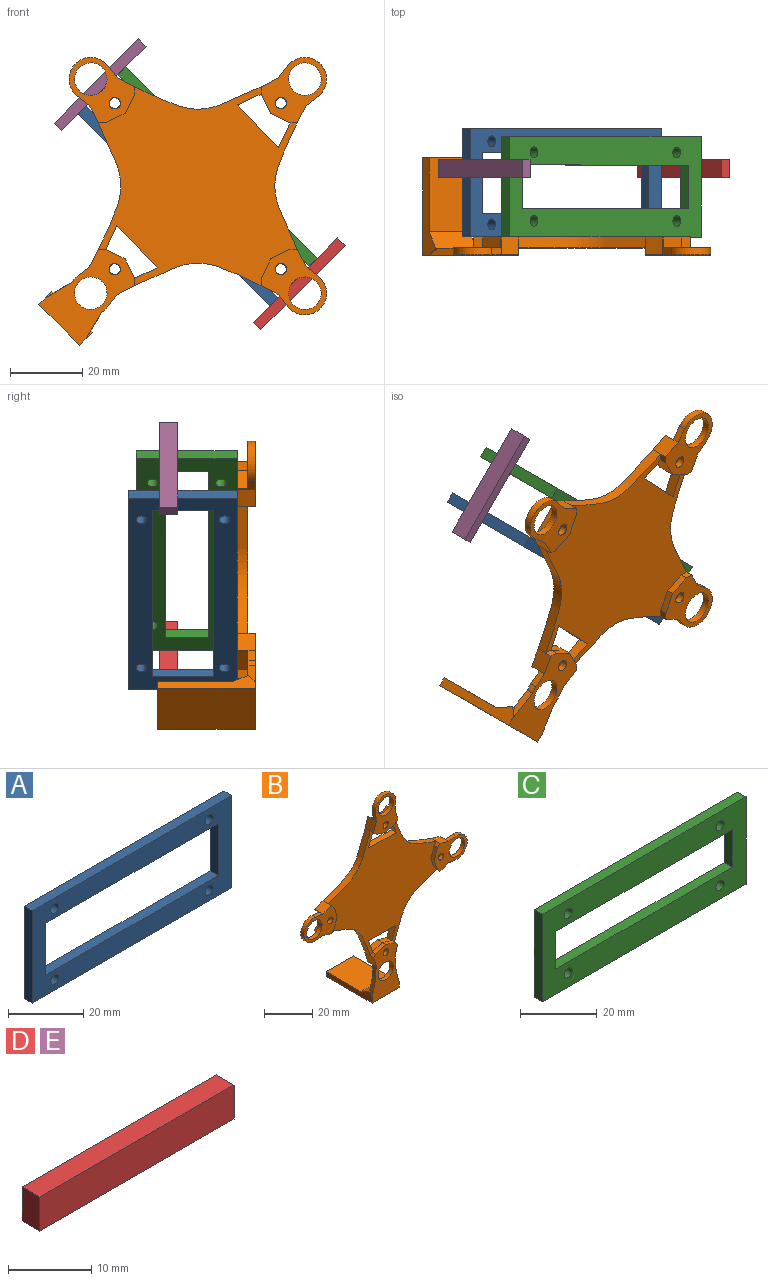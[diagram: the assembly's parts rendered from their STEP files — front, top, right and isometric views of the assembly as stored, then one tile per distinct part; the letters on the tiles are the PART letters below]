
ASSEMBLY  parts=5 mates=4
PART A: 14 faces, bbox 75x3x30 mm
  f0: plane 65x3mm, normal (0,0,-1), area 195mm2, adj f1,f11,f12,f13
  f1: plane 16.92x3mm, normal (-1,0,0), area 50.7mm2, adj f0,f2,f12,f13
  f2: plane 65x3mm, normal (0,0,1), area 195mm2, adj f1,f11,f12,f13
  f3: plane 30x3mm, normal (1,0,0), area 90mm2, adj f4,f10,f12,f13
  f4: plane 75x3mm, normal (0,0,1), area 225mm2, adj f3,f5,f12,f13
  f5: plane 30x3mm, normal (-1,0,0), area 90mm2, adj f4,f10,f12,f13
  f6: cylinder r=1.5mm len=3mm, axis (0,1,0), area 28.3mm2, adj f12,f13
  f7: cylinder r=1.5mm len=3mm, axis (0,1,0), area 28.3mm2, adj f12,f13
  f8: cylinder r=1.5mm len=3mm, axis (0,1,0), area 28.3mm2, adj f12,f13
  f9: cylinder r=1.5mm len=3mm, axis (0,1,0), area 28.3mm2, adj f12,f13
  f10: plane 75x3mm, normal (0,0,-1), area 225mm2, adj f3,f5,f12,f13
  f11: plane 16.92x3mm, normal (1,0,0), area 50.7mm2, adj f0,f2,f12,f13
  f12: plane 75x30mm, normal (0,-1,0), area 1122.2mm2, adj f0,f1,f2,f3,f4,f5,f6,f7
  f13: plane 75x30mm, normal (0,1,0), area 1122.2mm2, adj f0,f1,f2,f3,f4,f5,f6,f7
PART B: 98 faces, bbox 95.8x27x102.2 mm
  f0: plane 14.7x13.89mm, normal (0,1,0), area 102.7mm2, adj f1,f2,f4,f24,f25,f26,f59,f60
  f1: plane 8.46x2.17mm, normal (0.97,0,0.25), area 14.7mm2, adj f0,f4,f68,f95,f97
  f2: plane 8.46x2.17mm, normal (-0.97,0,0.25), area 14.7mm2, adj f0,f60,f68,f96,f97
  f3: plane 20.47x16mm, normal (0,0,1), area 327.5mm2, adj f91,f92,f94,f97
  f4: cylinder r=6mm len=2.08mm, axis (0,1,0), area 4.2mm2, adj f0,f1,f61,f68
  f5: plane 3.18x3.18mm, normal (0,-1,0), area 0.8mm2, adj f43,f84
  f6: plane 3.18x3.18mm, normal (0,-1,0), area 0.8mm2, adj f45,f77
  f7: plane 63.64x63.64mm, normal (0,-1,0), area 2022.9mm2, adj f10,f16,f22,f28,f34,f35,f36,f37
  f8: plane 3.18x3.18mm, normal (0,-1,0), area 0.8mm2, adj f44,f65
  f9: plane 3.18x3.18mm, normal (0,-1,0), area 0.8mm2, adj f46,f53
  f10: extruded ~24.75x24.75mm, area 112.2mm2, adj f7,f11,f47,f48
  f11: plane 5.15x5mm, normal (0.96,0,0.3), area 26.9mm2, adj f10,f12,f48,f82,f83,f87
  f12: plane 3x1.94mm, normal (-0.64,0,0.77), area 7.6mm2, adj f11,f13,f48,f88
  f13: plane 7.07x3mm, normal (0,0,1), area 21.2mm2, adj f12,f14,f48,f88
  f14: plane 3x1.94mm, normal (0.64,0,0.77), area 7.6mm2, adj f13,f15,f48,f88
  f15: plane 5.15x5mm, normal (-0.96,0,0.3), area 26.9mm2, adj f14,f16,f48,f80,f81,f87
  f16: extruded ~24.75x24.75mm, area 112.2mm2, adj f7,f15,f17,f48
  f17: plane 5.15x5mm, normal (-0.3,0,0.96), area 26.9mm2, adj f16,f18,f48,f49,f54,f56
  f18: plane 3x1.94mm, normal (-0.77,0,-0.64), area 7.6mm2, adj f17,f19,f48,f57
  f19: plane 7.07x3mm, normal (-1,0,0), area 21.2mm2, adj f18,f20,f48,f57
  f20: plane 3x1.94mm, normal (-0.77,0,0.64), area 7.6mm2, adj f19,f21,f48,f57
  f21: plane 5.15x5mm, normal (-0.3,0,-0.96), area 26.9mm2, adj f20,f22,f48,f51,f52,f56
  f22: extruded ~24.75x24.75mm, area 112.2mm2, adj f7,f21,f23,f48
  f23: plane 5.15x5mm, normal (-0.96,0,-0.3), area 26.9mm2, adj f22,f24,f48,f59,f66,f68
  f24: plane 3x1.94mm, normal (0.64,0,-0.77), area 7.6mm2, adj f0,f23,f25,f48
  f25: plane 7.07x3mm, normal (0,0,-1), area 21.2mm2, adj f0,f24,f26,f48
  f26: plane 3x1.94mm, normal (-0.64,0,-0.77), area 7.6mm2, adj f0,f25,f27,f48
  f27: plane 5.15x5mm, normal (0.96,0,-0.3), area 26.9mm2, adj f26,f28,f48,f61,f62,f68
  f28: extruded ~24.75x24.75mm, area 112.2mm2, adj f7,f27,f29,f48
  f29: plane 5.15x5mm, normal (0.3,0,-0.96), area 26.9mm2, adj f28,f30,f48,f73,f74,f79
  f30: plane 3x1.94mm, normal (0.77,0,0.64), area 7.6mm2, adj f29,f31,f48,f69
  f31: plane 7.07x3mm, normal (1,0,0), area 21.2mm2, adj f30,f32,f48,f69
  f32: plane 3x1.94mm, normal (0.77,0,-0.64), area 7.6mm2, adj f31,f47,f48,f69
  f33: plane 5.66x3mm, normal (-0.3,0,0.95), area 17.8mm2, adj f34,f42,f48,f58
  f34: plane 6.88x3mm, normal (0.94,0,0.34), area 22mm2, adj f7,f33,f48,f90
  f35: plane 5.66x2mm, normal (0.95,0,-0.32), area 11.9mm2, adj f7,f36,f52,f56
  f36: plane 5.66x2mm, normal (0.95,0,0.32), area 11.9mm2, adj f7,f35,f54,f56
  f37: plane 6.73x3mm, normal (0.94,0,-0.34), area 21.5mm2, adj f7,f38,f48,f89
  f38: plane 5.66x5mm, normal (-0.32,0,-0.95), area 29.8mm2, adj f37,f39,f48,f81,f87
  f39: plane 5.66x5mm, normal (0.32,0,-0.95), area 29.8mm2, adj f38,f40,f48,f82,f87
  f40: plane 7.16x3mm, normal (-0.94,0,-0.34), area 22.9mm2, adj f7,f39,f48,f89
  f41: plane 6.53x3mm, normal (-0.94,0,0.34), area 20.8mm2, adj f7,f42,f48,f90
  f42: plane 5.66x3mm, normal (0.3,0,0.95), area 17.8mm2, adj f33,f41,f48,f58
  f43: cylinder r=1.5mm len=3mm, axis (0,1,0), area 28.3mm2, adj f5,f48
  f44: cylinder r=1.5mm len=3mm, axis (0,1,0), area 28.3mm2, adj f8,f48
  f45: cylinder r=1.5mm len=3mm, axis (0,1,0), area 28.3mm2, adj f6,f48
  f46: cylinder r=1.5mm len=3mm, axis (0,1,0), area 28.3mm2, adj f9,f48
  f47: plane 5.15x5mm, normal (0.3,0,0.96), area 26.9mm2, adj f10,f32,f48,f70,f76,f79
  f48: plane 73.93x73.93mm, normal (0,1,0), area 2309.4mm2, adj f10,f11,f12,f13,f14,f15,f16,f17
  f49: plane 4.28x2mm, normal (0.11,0,0.99), area 8.6mm2, adj f17,f50,f56,f57
  f50: cylinder r=6mm len=12mm, axis (0,1,0), area 40.4mm2, adj f49,f51,f56,f57
  f51: plane 4.28x2mm, normal (0.11,0,-0.99), area 8.6mm2, adj f21,f50,f56,f57
  f52: plane 2x1.41mm, normal (0.71,0,-0.71), area 4mm2, adj f7,f21,f35,f56
  f53: cylinder r=1.59mm len=3.18mm, axis (0,1,0), area 20mm2, adj f9,f56
  f54: plane 2x1.41mm, normal (0.71,0,0.71), area 4mm2, adj f7,f17,f36,f56
  f55: cylinder r=4.5mm len=9mm, axis (0,1,0), area 56.5mm2, adj f56,f57
  f56: plane 19.42x14.14mm, normal (0,-1,0), area 135.4mm2, adj f17,f21,f35,f36,f49,f50,f51,f52
  f57: plane 12.57x12mm, normal (0,1,0), area 64.5mm2, adj f18,f19,f20,f49,f50,f51,f55
  f58: plane 11.31x1.91mm, normal (0,1,0), area 0.6mm2, adj f33,f42,f63,f64
  f59: plane 4.28x2mm, normal (-0.99,0,0.11), area 8.6mm2, adj f0,f23,f60,f68
  f60: cylinder r=6mm len=2.08mm, axis (0,1,0), area 4.2mm2, adj f0,f2,f59,f68
  f61: plane 4.28x2mm, normal (0.99,0,0.11), area 8.6mm2, adj f0,f4,f27,f68
  f62: plane 2x1.41mm, normal (0.71,0,0.71), area 4mm2, adj f7,f27,f63,f68
  f63: plane 5.66x2mm, normal (0.32,0,0.95), area 11.9mm2, adj f58,f62,f64,f68
  f64: plane 5.66x2mm, normal (-0.32,0,0.95), area 11.9mm2, adj f58,f63,f66,f68
  f65: cylinder r=1.59mm len=3.18mm, axis (0,1,0), area 20mm2, adj f8,f68
  f66: plane 2x1.41mm, normal (-0.71,0,0.71), area 4mm2, adj f7,f23,f64,f68
  f67: cylinder r=4.5mm len=9mm, axis (0,1,0), area 56.5mm2, adj f0,f68
  f68: plane 25.79x16mm, normal (0,-1,0), area 252.6mm2, adj f1,f2,f4,f23,f27,f59,f60,f61
  f69: plane 12.57x12mm, normal (0,1,0), area 64.5mm2, adj f30,f31,f32,f74,f75,f76,f78
  f70: plane 2x1.41mm, normal (-0.71,0,0.71), area 4mm2, adj f7,f47,f71,f79
  f71: plane 5.66x2mm, normal (-0.95,0,0.32), area 11.9mm2, adj f7,f70,f72,f79
  f72: plane 5.66x2mm, normal (-0.95,0,-0.32), area 11.9mm2, adj f7,f71,f73,f79
  f73: plane 2x1.41mm, normal (-0.71,0,-0.71), area 4mm2, adj f7,f29,f72,f79
  f74: plane 4.28x2mm, normal (-0.11,0,-0.99), area 8.6mm2, adj f29,f69,f75,f79
  f75: cylinder r=6mm len=12mm, axis (0,1,0), area 40.4mm2, adj f69,f74,f76,f79
  f76: plane 4.28x2mm, normal (-0.11,0,0.99), area 8.6mm2, adj f47,f69,f75,f79
  f77: cylinder r=1.59mm len=3.18mm, axis (0,1,0), area 20mm2, adj f6,f79
  f78: cylinder r=4.5mm len=9mm, axis (0,1,0), area 56.5mm2, adj f69,f79
  f79: plane 19.42x14.14mm, normal (0,-1,0), area 135.4mm2, adj f29,f47,f70,f71,f72,f73,f74,f75
  f80: plane 4.28x2mm, normal (-0.99,0,-0.11), area 8.6mm2, adj f15,f85,f87,f88
  f81: plane 2x1.41mm, normal (-0.71,0,-0.71), area 4mm2, adj f7,f15,f38,f87
  f82: plane 2x1.41mm, normal (0.71,0,-0.71), area 4mm2, adj f7,f11,f39,f87
  f83: plane 4.28x2mm, normal (0.99,0,-0.11), area 8.6mm2, adj f11,f85,f87,f88
  f84: cylinder r=1.59mm len=3.18mm, axis (0,1,0), area 20mm2, adj f5,f87
  f85: cylinder r=6mm len=12mm, axis (0,1,0), area 40.4mm2, adj f80,f83,f87,f88
  f86: cylinder r=4.5mm len=9mm, axis (0,1,0), area 56.5mm2, adj f87,f88
  f87: plane 19.42x14.14mm, normal (0,-1,0), area 135.4mm2, adj f11,f15,f38,f39,f80,f81,f82,f83
  f88: plane 12.57x12mm, normal (0,1,0), area 64.5mm2, adj f12,f13,f14,f80,f83,f85,f86
  f89: plane 16.4x3mm, normal (0.03,0,1), area 49.2mm2, adj f7,f37,f40,f48
  f90: plane 16.22x3mm, normal (-0.02,0,-1), area 48.7mm2, adj f7,f34,f41,f48
  f91: plane 27x5.07mm, normal (-1,0,0), area 75.9mm2, adj f3,f68,f93,f94,f96,f97
  f92: plane 27x5.07mm, normal (1,0,0), area 75.9mm2, adj f3,f68,f93,f94,f95,f97
  f93: plane 27x16mm, normal (0,0,-1), area 432mm2, adj f68,f91,f92,f94
  f94: plane 16x2.5mm, normal (0,1,0), area 40mm2, adj f3,f91,f92,f93
  f95: plane 2.57x1.94mm, normal (0,-0.8,0.6), area 1.1mm2, adj f1,f92,f97
  f96: plane 2.57x1.94mm, normal (0,-0.8,0.6), area 1.1mm2, adj f2,f91,f97
  f97: plane 16x4.6mm, normal (0,0.49,0.87), area 83.2mm2, adj f0,f1,f2,f3,f91,f92,f95,f96
PART C: 14 faces, bbox 75x3x27.9 mm
  f0: plane 65x3mm, normal (0,0,-1), area 195mm2, adj f1,f11,f12,f13
  f1: plane 12x3mm, normal (-1,0,0), area 36mm2, adj f0,f2,f12,f13
  f2: plane 65x3mm, normal (0,0,1), area 195mm2, adj f1,f11,f12,f13
  f3: plane 27.87x3mm, normal (1,0,0), area 83.6mm2, adj f4,f10,f12,f13
  f4: plane 75x3mm, normal (0,0,1), area 225mm2, adj f3,f5,f12,f13
  f5: plane 27.87x3mm, normal (-1,0,0), area 83.6mm2, adj f4,f10,f12,f13
  f6: cylinder r=1.5mm len=3mm, axis (0,1,0), area 28.3mm2, adj f12,f13
  f7: cylinder r=1.5mm len=3mm, axis (0,1,0), area 28.3mm2, adj f12,f13
  f8: cylinder r=1.5mm len=3mm, axis (0,1,0), area 28.3mm2, adj f12,f13
  f9: cylinder r=1.5mm len=3mm, axis (0,1,0), area 28.3mm2, adj f12,f13
  f10: plane 75x3mm, normal (0,0,-1), area 225mm2, adj f3,f5,f12,f13
  f11: plane 12x3mm, normal (1,0,0), area 36mm2, adj f0,f2,f12,f13
  f12: plane 75x27.87mm, normal (0,-1,0), area 1281.7mm2, adj f0,f1,f2,f3,f4,f5,f6,f7
  f13: plane 75x27.87mm, normal (0,1,0), area 1281.7mm2, adj f0,f1,f2,f3,f4,f5,f6,f7
PART D: 6 faces, bbox 33x3x5 mm
  f0: plane 5x3mm, normal (1,0,0), area 15mm2, adj f1,f3,f4,f5
  f1: plane 33x3mm, normal (0,0,1), area 99mm2, adj f0,f2,f4,f5
  f2: plane 5x3mm, normal (-1,0,0), area 15mm2, adj f1,f3,f4,f5
  f3: plane 33x3mm, normal (0,0,-1), area 99mm2, adj f0,f2,f4,f5
  f4: plane 33x5mm, normal (0,-1,0), area 165mm2, adj f0,f1,f2,f3
  f5: plane 33x5mm, normal (0,1,0), area 165mm2, adj f0,f1,f2,f3
PART E: same geometry as D
PLACE A rot(axis=(-0.86,0.36,0.36),98.4deg) t=(-5.6,-7.57,7.09)mm
PLACE B rot(axis=(0,1,0),45deg) t=(-28.68,-22.57,1.37)mm
PLACE C rot(axis=(-0.86,0.36,0.36),98.4deg) t=(5.36,-8.63,18.05)mm
PLACE D rot(axis=(0.86,-0.36,0.36),98.4deg) t=(27.99,-3.63,-12.36)mm
PLACE E rot(axis=(-0.86,-0.36,-0.36),98.4deg) t=(-25.04,-3.63,40.68)mm
MATE fastened D.f5 <-> C.f3  axis (-0.71,0,0.71) through (27.99,-3.63,-12.36)mm
MATE fastened C.f10 <-> B.f48  axis (0,-1,0) through (6.42,-22.57,19.11)mm
MATE fastened A.f10 <-> B.f48  axis (0,-1,0) through (-4.54,-22.57,8.15)mm
MATE fastened E.f5 <-> C.f5  axis (0.71,0,-0.71) through (-25.04,-3.63,40.68)mm
